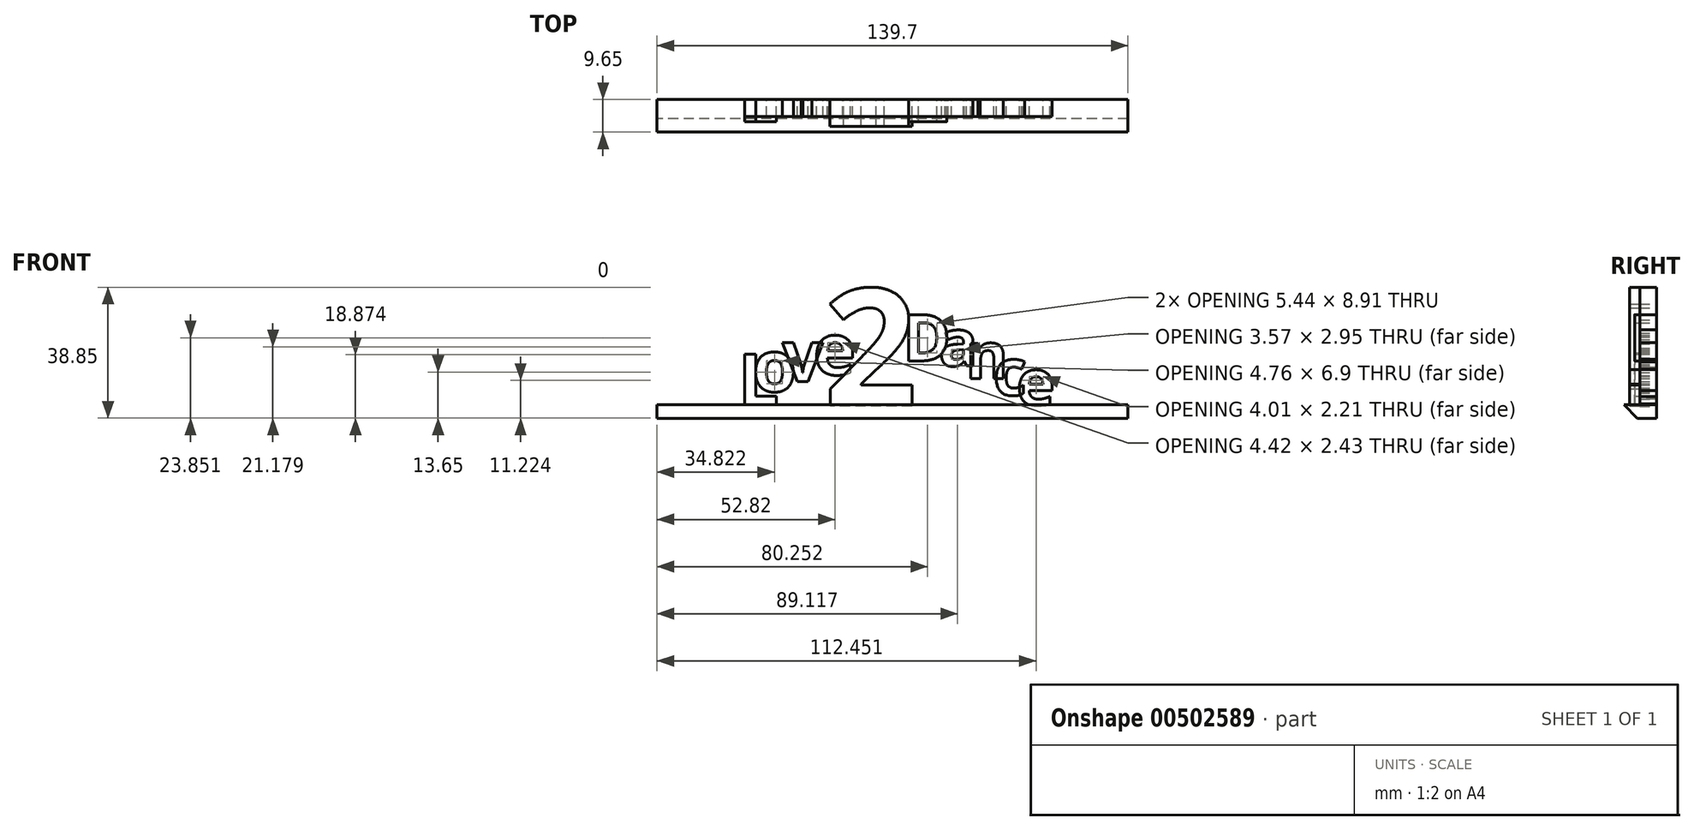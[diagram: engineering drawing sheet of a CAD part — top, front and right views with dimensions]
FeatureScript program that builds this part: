
annotation { "Feature Type Name" : "Feature", "Feature Type Description" : "" }
export const myFeature = defineFeature(function(context is Context, id is Id, definition is map)
    precondition{}
    {
        {
            var Q0;
            Q0=qCreatedBy(makeId("Front.planeOp"),FACE);
            var sketch = newSketch(context, id + "F0", { "sketchPlane" : qUnion([Q0])});
            skText(sketch, "E0", { "text": "Love", "fontName": "NotoSans-Bold.ttf"});
            skText(sketch, "E1", { "text": "2", "fontName": "OpenSans-Bold.ttf"});
            skText(sketch, "E2", { "text": "Dance", "fontName": "OpenSans-Bold.ttf"});
            const initialGuessF0  = {"E0": [-0.06167, 0.00278, 1, 0, 0.01522], "E1": [-0.01508, 0.00025, 1, 0, 0.035], "E2": [0.0105, 0.0027, 1, 0, 0.0138]};
            skSetInitialGuess(sketch, initialGuessF0);
            skSolve(sketch);
        }
        {
            var Q0;
            Q0 = qSketchRegion(id + "F0", true);
            extrude(context, id + "F1", {"entities" : qUnion([Q0]), "depth" : 5 * mm});
        }
        {
            var Q0;
            Q0=makeQuery(id+"F1.opExtrude","SWEPT_BODY",BODY,{"disambiguationData":[OSD([sQuery(id+"F0.wireOp",EDGE,"E0.sketch_text.stroke-34"),sQuery(id+"F0.wireOp",EDGE,"E0.sketch_text.stroke-35"),sQuery(id+"F0.wireOp",EDGE,"E0.sketch_text.stroke-36"),sQuery(id+"F0.wireOp",EDGE,"E0.sketch_text.stroke-37"),sQuery(id+"F0.wireOp",EDGE,"E0.sketch_text.stroke-38"),sQuery(id+"F0.wireOp",EDGE,"E0.sketch_text.stroke-39"),sQuery(id+"F0.wireOp",EDGE,"E0.sketch_text.stroke-40"),sQuery(id+"F0.wireOp",EDGE,"E0.sketch_text.stroke-41"),sQuery(id+"F0.wireOp",EDGE,"E0.sketch_text.stroke-42"),sQuery(id+"F0.wireOp",EDGE,"E0.sketch_text.stroke-43"),sQuery(id+"F0.wireOp",EDGE,"E0.sketch_text.stroke-44"),sQuery(id+"F0.wireOp",EDGE,"E0.sketch_text.stroke-45"),sQuery(id+"F0.wireOp",EDGE,"E0.sketch_text.stroke-46"),sQuery(id+"F0.wireOp",EDGE,"E0.sketch_text.stroke-47"),sQuery(id+"F0.wireOp",EDGE,"E0.sketch_text.stroke-48"),sQuery(id+"F0.wireOp",EDGE,"E0.sketch_text.stroke-49"),sQuery(id+"F0.wireOp",EDGE,"E0.sketch_text.stroke-50"),sQuery(id+"F0.wireOp",EDGE,"E0.sketch_text.stroke-51"),sQuery(id+"F0.wireOp",EDGE,"E0.sketch_text.stroke-52"),sQuery(id+"F0.wireOp",EDGE,"E0.sketch_text.stroke-53")])]});
            transform(context, id + "F2", {"entities" : qUnion([Q0]), "transformType" : TransformType.TRANSLATION_3D, "dx" : 6.2 * mm, "dy" : 0 * mm, "dz" : 7 * mm, "makeCopy" : false});
        }
        {
            var Q0;
            Q0=makeQuery(id+"F1.opExtrude","SWEPT_BODY",BODY,{"disambiguationData":[OSD([sQuery(id+"F0.wireOp",EDGE,"E0.sketch_text.stroke-24"),sQuery(id+"F0.wireOp",EDGE,"E0.sketch_text.stroke-25"),sQuery(id+"F0.wireOp",EDGE,"E0.sketch_text.stroke-26"),sQuery(id+"F0.wireOp",EDGE,"E0.sketch_text.stroke-27"),sQuery(id+"F0.wireOp",EDGE,"E0.sketch_text.stroke-28"),sQuery(id+"F0.wireOp",EDGE,"E0.sketch_text.stroke-29"),sQuery(id+"F0.wireOp",EDGE,"E0.sketch_text.stroke-30"),sQuery(id+"F0.wireOp",EDGE,"E0.sketch_text.stroke-31"),sQuery(id+"F0.wireOp",EDGE,"E0.sketch_text.stroke-32"),sQuery(id+"F0.wireOp",EDGE,"E0.sketch_text.stroke-33")])]});
            transform(context, id + "F3", {"entities" : qUnion([Q0]), "transformType" : TransformType.TRANSLATION_3D, "dx" : 9 * mm, "dy" : 0 * mm, "dz" : 5 * mm, "makeCopy" : false});
        }
        {
            var Q0;
            Q0=makeQuery(id+"F1.opExtrude","SWEPT_BODY",BODY,{"disambiguationData":[OSD([sQuery(id+"F0.wireOp",EDGE,"E0.sketch_text.stroke-6"),sQuery(id+"F0.wireOp",EDGE,"E0.sketch_text.stroke-7"),sQuery(id+"F0.wireOp",EDGE,"E0.sketch_text.stroke-8"),sQuery(id+"F0.wireOp",EDGE,"E0.sketch_text.stroke-9"),sQuery(id+"F0.wireOp",EDGE,"E0.sketch_text.stroke-10"),sQuery(id+"F0.wireOp",EDGE,"E0.sketch_text.stroke-11"),sQuery(id+"F0.wireOp",EDGE,"E0.sketch_text.stroke-12"),sQuery(id+"F0.wireOp",EDGE,"E0.sketch_text.stroke-13"),sQuery(id+"F0.wireOp",EDGE,"E0.sketch_text.stroke-14"),sQuery(id+"F0.wireOp",EDGE,"E0.sketch_text.stroke-15"),sQuery(id+"F0.wireOp",EDGE,"E0.sketch_text.stroke-16"),sQuery(id+"F0.wireOp",EDGE,"E0.sketch_text.stroke-17"),sQuery(id+"F0.wireOp",EDGE,"E0.sketch_text.stroke-18"),sQuery(id+"F0.wireOp",EDGE,"E0.sketch_text.stroke-19"),sQuery(id+"F0.wireOp",EDGE,"E0.sketch_text.stroke-20"),sQuery(id+"F0.wireOp",EDGE,"E0.sketch_text.stroke-21"),sQuery(id+"F0.wireOp",EDGE,"E0.sketch_text.stroke-22"),sQuery(id+"F0.wireOp",EDGE,"E0.sketch_text.stroke-23")])]});
            transform(context, id + "F4", {"entities" : qUnion([Q0]), "transformType" : TransformType.TRANSLATION_3D, "dx" : 13.2 * mm, "dy" : 0 * mm, "dz" : 2 * mm, "makeCopy" : false});
        }
        {
            var Q0;
            Q0=makeQuery(id+"F1.opExtrude","SWEPT_BODY",BODY,{"disambiguationData":[OSD([sQuery(id+"F0.wireOp",EDGE,"E0.sketch_text.stroke-0"),sQuery(id+"F0.wireOp",EDGE,"E0.sketch_text.stroke-1"),sQuery(id+"F0.wireOp",EDGE,"E0.sketch_text.stroke-2"),sQuery(id+"F0.wireOp",EDGE,"E0.sketch_text.stroke-3"),sQuery(id+"F0.wireOp",EDGE,"E0.sketch_text.stroke-4"),sQuery(id+"F0.wireOp",EDGE,"E0.sketch_text.stroke-5")])]});
            transform(context, id + "F5", {"entities" : qUnion([Q0]), "transformType" : TransformType.TRANSLATION_3D, "dx" : 21 * mm, "dy" : 0 * mm, "dz" : -2 * mm, "makeCopy" : false});
        }
        {
            var Q0;
            Q0=makeQuery(id+"F1.opExtrude","SWEPT_BODY",BODY,{"disambiguationData":[OSD([sQuery(id+"F0.wireOp",EDGE,"E2.sketch_text.stroke-0"),sQuery(id+"F0.wireOp",EDGE,"E2.sketch_text.stroke-1"),sQuery(id+"F0.wireOp",EDGE,"E2.sketch_text.stroke-2"),sQuery(id+"F0.wireOp",EDGE,"E2.sketch_text.stroke-3"),sQuery(id+"F0.wireOp",EDGE,"E2.sketch_text.stroke-4"),sQuery(id+"F0.wireOp",EDGE,"E2.sketch_text.stroke-5"),sQuery(id+"F0.wireOp",EDGE,"E2.sketch_text.stroke-6"),sQuery(id+"F0.wireOp",EDGE,"E2.sketch_text.stroke-7"),sQuery(id+"F0.wireOp",EDGE,"E2.sketch_text.stroke-8"),sQuery(id+"F0.wireOp",EDGE,"E2.sketch_text.stroke-9"),sQuery(id+"F0.wireOp",EDGE,"E2.sketch_text.stroke-10"),sQuery(id+"F0.wireOp",EDGE,"E2.sketch_text.stroke-11")])]});
            transform(context, id + "F6", {"entities" : qUnion([Q0]), "transformType" : TransformType.TRANSLATION_3D, "dx" : -2.4 * mm, "dy" : 0 * mm, "dz" : 11.2 * mm, "makeCopy" : false});
        }
        {
            var Q0;
            Q0=makeQuery(id+"F1.opExtrude","SWEPT_BODY",BODY,{"disambiguationData":[OSD([sQuery(id+"F0.wireOp",EDGE,"E2.sketch_text.stroke-12"),sQuery(id+"F0.wireOp",EDGE,"E2.sketch_text.stroke-13"),sQuery(id+"F0.wireOp",EDGE,"E2.sketch_text.stroke-14"),sQuery(id+"F0.wireOp",EDGE,"E2.sketch_text.stroke-15"),sQuery(id+"F0.wireOp",EDGE,"E2.sketch_text.stroke-16"),sQuery(id+"F0.wireOp",EDGE,"E2.sketch_text.stroke-17"),sQuery(id+"F0.wireOp",EDGE,"E2.sketch_text.stroke-18"),sQuery(id+"F0.wireOp",EDGE,"E2.sketch_text.stroke-19"),sQuery(id+"F0.wireOp",EDGE,"E2.sketch_text.stroke-20"),sQuery(id+"F0.wireOp",EDGE,"E2.sketch_text.stroke-21"),sQuery(id+"F0.wireOp",EDGE,"E2.sketch_text.stroke-22"),sQuery(id+"F0.wireOp",EDGE,"E2.sketch_text.stroke-23"),sQuery(id+"F0.wireOp",EDGE,"E2.sketch_text.stroke-24"),sQuery(id+"F0.wireOp",EDGE,"E2.sketch_text.stroke-25"),sQuery(id+"F0.wireOp",EDGE,"E2.sketch_text.stroke-26"),sQuery(id+"F0.wireOp",EDGE,"E2.sketch_text.stroke-27"),sQuery(id+"F0.wireOp",EDGE,"E2.sketch_text.stroke-28"),sQuery(id+"F0.wireOp",EDGE,"E2.sketch_text.stroke-29"),sQuery(id+"F0.wireOp",EDGE,"E2.sketch_text.stroke-30"),sQuery(id+"F0.wireOp",EDGE,"E2.sketch_text.stroke-31"),sQuery(id+"F0.wireOp",EDGE,"E2.sketch_text.stroke-32"),sQuery(id+"F0.wireOp",EDGE,"E2.sketch_text.stroke-33"),sQuery(id+"F0.wireOp",EDGE,"E2.sketch_text.stroke-34"),sQuery(id+"F0.wireOp",EDGE,"E2.sketch_text.stroke-35"),sQuery(id+"F0.wireOp",EDGE,"E2.sketch_text.stroke-36")])]});
            transform(context, id + "F7", {"entities" : qUnion([Q0]), "transformType" : TransformType.TRANSLATION_3D, "dx" : -5.9 * mm, "dy" : 0 * mm, "dz" : 9.7 * mm, "makeCopy" : false});
        }
        {
            var Q0;
            Q0=makeQuery(id+"F1.opExtrude","SWEPT_BODY",BODY,{"disambiguationData":[OSD([sQuery(id+"F0.wireOp",EDGE,"E2.sketch_text.stroke-37"),sQuery(id+"F0.wireOp",EDGE,"E2.sketch_text.stroke-38"),sQuery(id+"F0.wireOp",EDGE,"E2.sketch_text.stroke-39"),sQuery(id+"F0.wireOp",EDGE,"E2.sketch_text.stroke-40"),sQuery(id+"F0.wireOp",EDGE,"E2.sketch_text.stroke-41"),sQuery(id+"F0.wireOp",EDGE,"E2.sketch_text.stroke-42"),sQuery(id+"F0.wireOp",EDGE,"E2.sketch_text.stroke-43"),sQuery(id+"F0.wireOp",EDGE,"E2.sketch_text.stroke-44"),sQuery(id+"F0.wireOp",EDGE,"E2.sketch_text.stroke-45"),sQuery(id+"F0.wireOp",EDGE,"E2.sketch_text.stroke-46"),sQuery(id+"F0.wireOp",EDGE,"E2.sketch_text.stroke-47"),sQuery(id+"F0.wireOp",EDGE,"E2.sketch_text.stroke-48"),sQuery(id+"F0.wireOp",EDGE,"E2.sketch_text.stroke-49"),sQuery(id+"F0.wireOp",EDGE,"E2.sketch_text.stroke-50"),sQuery(id+"F0.wireOp",EDGE,"E2.sketch_text.stroke-51"),sQuery(id+"F0.wireOp",EDGE,"E2.sketch_text.stroke-52"),sQuery(id+"F0.wireOp",EDGE,"E2.sketch_text.stroke-53")])]});
            transform(context, id + "F8", {"entities" : qUnion([Q0]), "transformType" : TransformType.TRANSLATION_3D, "dx" : -9.5 * mm, "dy" : 0 * mm, "dz" : 5.9 * mm, "makeCopy" : false});
        }
        {
            var Q0;
            Q0=makeQuery(id+"F1.opExtrude","SWEPT_BODY",BODY,{"disambiguationData":[OSD([sQuery(id+"F0.wireOp",EDGE,"E2.sketch_text.stroke-54"),sQuery(id+"F0.wireOp",EDGE,"E2.sketch_text.stroke-55"),sQuery(id+"F0.wireOp",EDGE,"E2.sketch_text.stroke-56"),sQuery(id+"F0.wireOp",EDGE,"E2.sketch_text.stroke-57"),sQuery(id+"F0.wireOp",EDGE,"E2.sketch_text.stroke-58"),sQuery(id+"F0.wireOp",EDGE,"E2.sketch_text.stroke-59"),sQuery(id+"F0.wireOp",EDGE,"E2.sketch_text.stroke-60"),sQuery(id+"F0.wireOp",EDGE,"E2.sketch_text.stroke-61"),sQuery(id+"F0.wireOp",EDGE,"E2.sketch_text.stroke-62"),sQuery(id+"F0.wireOp",EDGE,"E2.sketch_text.stroke-63"),sQuery(id+"F0.wireOp",EDGE,"E2.sketch_text.stroke-64"),sQuery(id+"F0.wireOp",EDGE,"E2.sketch_text.stroke-65"),sQuery(id+"F0.wireOp",EDGE,"E2.sketch_text.stroke-66"),sQuery(id+"F0.wireOp",EDGE,"E2.sketch_text.stroke-67")])]});
            transform(context, id + "F9", {"entities" : qUnion([Q0]), "transformType" : TransformType.TRANSLATION_3D, "dx" : -13.9 * mm, "dy" : 0 * mm, "dz" : 1 * mm, "makeCopy" : false});
        }
        {
            var Q0;
            Q0=makeQuery(id+"F1.opExtrude","SWEPT_BODY",BODY,{"disambiguationData":[OSD([sQuery(id+"F0.wireOp",EDGE,"E0.sketch_text.stroke-34"),sQuery(id+"F0.wireOp",EDGE,"E0.sketch_text.stroke-35"),sQuery(id+"F0.wireOp",EDGE,"E0.sketch_text.stroke-36"),sQuery(id+"F0.wireOp",EDGE,"E0.sketch_text.stroke-37"),sQuery(id+"F0.wireOp",EDGE,"E0.sketch_text.stroke-38"),sQuery(id+"F0.wireOp",EDGE,"E0.sketch_text.stroke-39"),sQuery(id+"F0.wireOp",EDGE,"E0.sketch_text.stroke-40"),sQuery(id+"F0.wireOp",EDGE,"E0.sketch_text.stroke-41"),sQuery(id+"F0.wireOp",EDGE,"E0.sketch_text.stroke-42"),sQuery(id+"F0.wireOp",EDGE,"E0.sketch_text.stroke-43"),sQuery(id+"F0.wireOp",EDGE,"E0.sketch_text.stroke-44"),sQuery(id+"F0.wireOp",EDGE,"E0.sketch_text.stroke-45"),sQuery(id+"F0.wireOp",EDGE,"E0.sketch_text.stroke-46"),sQuery(id+"F0.wireOp",EDGE,"E0.sketch_text.stroke-47"),sQuery(id+"F0.wireOp",EDGE,"E0.sketch_text.stroke-48"),sQuery(id+"F0.wireOp",EDGE,"E0.sketch_text.stroke-49"),sQuery(id+"F0.wireOp",EDGE,"E0.sketch_text.stroke-50"),sQuery(id+"F0.wireOp",EDGE,"E0.sketch_text.stroke-51"),sQuery(id+"F0.wireOp",EDGE,"E0.sketch_text.stroke-52"),sQuery(id+"F0.wireOp",EDGE,"E0.sketch_text.stroke-53"),sQuery(id+"F0.wireOp",EDGE,"E1.sketch_text.stroke-0"),sQuery(id+"F0.wireOp",EDGE,"E1.sketch_text.stroke-1"),sQuery(id+"F0.wireOp",EDGE,"E1.sketch_text.stroke-2"),sQuery(id+"F0.wireOp",EDGE,"E1.sketch_text.stroke-3"),sQuery(id+"F0.wireOp",EDGE,"E1.sketch_text.stroke-4"),sQuery(id+"F0.wireOp",EDGE,"E1.sketch_text.stroke-5"),sQuery(id+"F0.wireOp",EDGE,"E1.sketch_text.stroke-6"),sQuery(id+"F0.wireOp",EDGE,"E1.sketch_text.stroke-7"),sQuery(id+"F0.wireOp",EDGE,"E1.sketch_text.stroke-8"),sQuery(id+"F0.wireOp",EDGE,"E1.sketch_text.stroke-9"),sQuery(id+"F0.wireOp",EDGE,"E1.sketch_text.stroke-10"),sQuery(id+"F0.wireOp",EDGE,"E1.sketch_text.stroke-11"),sQuery(id+"F0.wireOp",EDGE,"E1.sketch_text.stroke-12"),sQuery(id+"F0.wireOp",EDGE,"E1.sketch_text.stroke-13"),sQuery(id+"F0.wireOp",EDGE,"E1.sketch_text.stroke-14"),sQuery(id+"F0.wireOp",EDGE,"E1.sketch_text.stroke-15"),sQuery(id+"F0.wireOp",EDGE,"E1.sketch_text.stroke-16"),sQuery(id+"F0.wireOp",EDGE,"E1.sketch_text.stroke-17"),sQuery(id+"F0.wireOp",EDGE,"E1.sketch_text.stroke-18"),sQuery(id+"F0.wireOp",EDGE,"E1.sketch_text.stroke-19"),sQuery(id+"F0.wireOp",EDGE,"E1.sketch_text.stroke-20"),sQuery(id+"F0.wireOp",EDGE,"E1.sketch_text.stroke-21"),sQuery(id+"F0.wireOp",EDGE,"E1.sketch_text.stroke-22"),sQuery(id+"F0.wireOp",EDGE,"E1.sketch_text.stroke-23")])]});
            transform(context, id + "F10", {"entities" : qUnion([Q0]), "transformType" : TransformType.TRANSLATION_3D, "dx" : -12.5 * mm, "dy" : 0 * mm, "dz" : -2 * mm, "makeCopy" : false});
        }
        {
            var Q0;
            Q0=makeQuery(id+"F1.opExtrude","SWEPT_BODY",BODY,{"disambiguationData":[OSD([sQuery(id+"F0.wireOp",EDGE,"E1.sketch_text.stroke-0"),sQuery(id+"F0.wireOp",EDGE,"E1.sketch_text.stroke-1"),sQuery(id+"F0.wireOp",EDGE,"E1.sketch_text.stroke-2"),sQuery(id+"F0.wireOp",EDGE,"E1.sketch_text.stroke-3"),sQuery(id+"F0.wireOp",EDGE,"E1.sketch_text.stroke-4"),sQuery(id+"F0.wireOp",EDGE,"E1.sketch_text.stroke-5"),sQuery(id+"F0.wireOp",EDGE,"E1.sketch_text.stroke-6"),sQuery(id+"F0.wireOp",EDGE,"E1.sketch_text.stroke-7"),sQuery(id+"F0.wireOp",EDGE,"E1.sketch_text.stroke-8"),sQuery(id+"F0.wireOp",EDGE,"E1.sketch_text.stroke-9"),sQuery(id+"F0.wireOp",EDGE,"E1.sketch_text.stroke-10"),sQuery(id+"F0.wireOp",EDGE,"E1.sketch_text.stroke-11"),sQuery(id+"F0.wireOp",EDGE,"E1.sketch_text.stroke-12"),sQuery(id+"F0.wireOp",EDGE,"E1.sketch_text.stroke-13"),sQuery(id+"F0.wireOp",EDGE,"E1.sketch_text.stroke-14"),sQuery(id+"F0.wireOp",EDGE,"E1.sketch_text.stroke-15"),sQuery(id+"F0.wireOp",EDGE,"E1.sketch_text.stroke-16"),sQuery(id+"F0.wireOp",EDGE,"E1.sketch_text.stroke-17"),sQuery(id+"F0.wireOp",EDGE,"E1.sketch_text.stroke-18"),sQuery(id+"F0.wireOp",EDGE,"E1.sketch_text.stroke-19"),sQuery(id+"F0.wireOp",EDGE,"E1.sketch_text.stroke-20"),sQuery(id+"F0.wireOp",EDGE,"E1.sketch_text.stroke-21"),sQuery(id+"F0.wireOp",EDGE,"E1.sketch_text.stroke-22"),sQuery(id+"F0.wireOp",EDGE,"E1.sketch_text.stroke-23")])]});
            transform(context, id + "F11", {"entities" : qUnion([Q0]), "transformType" : TransformType.TRANSLATION_3D, "dx" : 12.2 * mm, "dy" : 0 * mm, "dz" : 2.3 * mm, "makeCopy" : false});
        }
        {
            var Q0;
            Q0=makeQuery(id+"F1.opExtrude","SWEPT_BODY",BODY,{"disambiguationData":[OSD([sQuery(id+"F0.wireOp",EDGE,"E2.sketch_text.stroke-68"),sQuery(id+"F0.wireOp",EDGE,"E2.sketch_text.stroke-69"),sQuery(id+"F0.wireOp",EDGE,"E2.sketch_text.stroke-70"),sQuery(id+"F0.wireOp",EDGE,"E2.sketch_text.stroke-71"),sQuery(id+"F0.wireOp",EDGE,"E2.sketch_text.stroke-72"),sQuery(id+"F0.wireOp",EDGE,"E2.sketch_text.stroke-73"),sQuery(id+"F0.wireOp",EDGE,"E2.sketch_text.stroke-74"),sQuery(id+"F0.wireOp",EDGE,"E2.sketch_text.stroke-75"),sQuery(id+"F0.wireOp",EDGE,"E2.sketch_text.stroke-76"),sQuery(id+"F0.wireOp",EDGE,"E2.sketch_text.stroke-77"),sQuery(id+"F0.wireOp",EDGE,"E2.sketch_text.stroke-78"),sQuery(id+"F0.wireOp",EDGE,"E2.sketch_text.stroke-79"),sQuery(id+"F0.wireOp",EDGE,"E2.sketch_text.stroke-80"),sQuery(id+"F0.wireOp",EDGE,"E2.sketch_text.stroke-81"),sQuery(id+"F0.wireOp",EDGE,"E2.sketch_text.stroke-82"),sQuery(id+"F0.wireOp",EDGE,"E2.sketch_text.stroke-83"),sQuery(id+"F0.wireOp",EDGE,"E2.sketch_text.stroke-84"),sQuery(id+"F0.wireOp",EDGE,"E2.sketch_text.stroke-85"),sQuery(id+"F0.wireOp",EDGE,"E2.sketch_text.stroke-86"),sQuery(id+"F0.wireOp",EDGE,"E2.sketch_text.stroke-87")])]});
            transform(context, id + "F12", {"entities" : qUnion([Q0]), "transformType" : TransformType.TRANSLATION_3D, "dx" : -16.9 * mm, "dy" : 0 * mm, "dz" : -2.1 * mm, "makeCopy" : false});
        }
        {
            var Q0;
            Q0=qCreatedBy(makeId("Front.planeOp"),FACE);
            var sketch = newSketch(context, id + "F13", { "sketchPlane" : qUnion([Q0])});
            skLineSegment(sketch, "E3.bottom", {"start": v(-64.8, 0.85) * mm, "end": v(74.9, 0.85) * mm});
            skLineSegment(sketch, "E3.top", {"start": v(-64.8, -3.1) * mm, "end": v(74.9, -3.1) * mm});
            skLineSegment(sketch, "E3.left", {"start": v(-64.8, 0.85) * mm, "end": v(-64.8, -3.1) * mm});
            skLineSegment(sketch, "E3.right", {"start": v(74.9, 0.85) * mm, "end": v(74.9, -3.1) * mm});
            skSolve(sketch);
        }
        {
            var Q0;
            Q0 = qSketchRegion(id + "F13", true);
            extrude(context, id + "F14", {"entities" : qUnion([Q0]), "depth" : 9.7 * mm});
        }
        {
            var Q0;
            Q0=makeQuery(id+"F1.opExtrude","CAP_FACE",FACE,{"disambiguationData":[OSD([sQuery(id+"F0.wireOp",EDGE,"E1.sketch_text.stroke-0"),sQuery(id+"F0.wireOp",EDGE,"E1.sketch_text.stroke-1"),sQuery(id+"F0.wireOp",EDGE,"E1.sketch_text.stroke-2"),sQuery(id+"F0.wireOp",EDGE,"E1.sketch_text.stroke-3"),sQuery(id+"F0.wireOp",EDGE,"E1.sketch_text.stroke-4"),sQuery(id+"F0.wireOp",EDGE,"E1.sketch_text.stroke-5"),sQuery(id+"F0.wireOp",EDGE,"E1.sketch_text.stroke-6"),sQuery(id+"F0.wireOp",EDGE,"E1.sketch_text.stroke-7"),sQuery(id+"F0.wireOp",EDGE,"E1.sketch_text.stroke-8"),sQuery(id+"F0.wireOp",EDGE,"E1.sketch_text.stroke-9"),sQuery(id+"F0.wireOp",EDGE,"E1.sketch_text.stroke-10"),sQuery(id+"F0.wireOp",EDGE,"E1.sketch_text.stroke-11"),sQuery(id+"F0.wireOp",EDGE,"E1.sketch_text.stroke-12"),sQuery(id+"F0.wireOp",EDGE,"E1.sketch_text.stroke-13"),sQuery(id+"F0.wireOp",EDGE,"E1.sketch_text.stroke-14"),sQuery(id+"F0.wireOp",EDGE,"E1.sketch_text.stroke-15"),sQuery(id+"F0.wireOp",EDGE,"E1.sketch_text.stroke-16"),sQuery(id+"F0.wireOp",EDGE,"E1.sketch_text.stroke-17"),sQuery(id+"F0.wireOp",EDGE,"E1.sketch_text.stroke-18"),sQuery(id+"F0.wireOp",EDGE,"E1.sketch_text.stroke-19"),sQuery(id+"F0.wireOp",EDGE,"E1.sketch_text.stroke-20"),sQuery(id+"F0.wireOp",EDGE,"E1.sketch_text.stroke-21"),sQuery(id+"F0.wireOp",EDGE,"E1.sketch_text.stroke-22"),sQuery(id+"F0.wireOp",EDGE,"E1.sketch_text.stroke-23")])],"isStart":false});
            extrude(context, id + "F15", {"entities" : qUnion([Q0]), "depth" : 3 * mm});
        }
        {
            var Q0;
            Q0=makeQuery(id+"F1.opExtrude","CAP_FACE",FACE,{"disambiguationData":[OSD([sQuery(id+"F0.wireOp",EDGE,"E0.sketch_text.stroke-0"),sQuery(id+"F0.wireOp",EDGE,"E0.sketch_text.stroke-1"),sQuery(id+"F0.wireOp",EDGE,"E0.sketch_text.stroke-2"),sQuery(id+"F0.wireOp",EDGE,"E0.sketch_text.stroke-3"),sQuery(id+"F0.wireOp",EDGE,"E0.sketch_text.stroke-4"),sQuery(id+"F0.wireOp",EDGE,"E0.sketch_text.stroke-5")])],"isStart":false});
            extrude(context, id + "F16", {"entities" : qUnion([Q0]), "depth" : 1.5 * mm});
        }
        {
            var Q0;
            Q0=makeQuery(id+"F1.opExtrude","CAP_FACE",FACE,{"disambiguationData":[OSD([sQuery(id+"F0.wireOp",EDGE,"E2.sketch_text.stroke-0"),sQuery(id+"F0.wireOp",EDGE,"E2.sketch_text.stroke-1"),sQuery(id+"F0.wireOp",EDGE,"E2.sketch_text.stroke-2"),sQuery(id+"F0.wireOp",EDGE,"E2.sketch_text.stroke-3"),sQuery(id+"F0.wireOp",EDGE,"E2.sketch_text.stroke-4"),sQuery(id+"F0.wireOp",EDGE,"E2.sketch_text.stroke-5"),sQuery(id+"F0.wireOp",EDGE,"E2.sketch_text.stroke-6"),sQuery(id+"F0.wireOp",EDGE,"E2.sketch_text.stroke-7"),sQuery(id+"F0.wireOp",EDGE,"E2.sketch_text.stroke-8"),sQuery(id+"F0.wireOp",EDGE,"E2.sketch_text.stroke-9"),sQuery(id+"F0.wireOp",EDGE,"E2.sketch_text.stroke-10"),sQuery(id+"F0.wireOp",EDGE,"E2.sketch_text.stroke-11")])],"isStart":false});
            extrude(context, id + "F17", {"entities" : qUnion([Q0]), "depth" : 1.5 * mm});
        }
        {
            var Q0;
            Q0=makeQuery(id+"F14.opExtrude","CAP_EDGE",EDGE,{"disambiguationData":[OSD([sQuery(id+"F13.wireOp",EDGE,"E3.top")])],"isStart":false});
            chamfer(context, id + "F18", {"entities" : qUnion([Q0]), "width" : 4 * mm, "tangentPropagation" : true});
        }
    });
